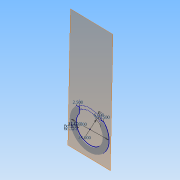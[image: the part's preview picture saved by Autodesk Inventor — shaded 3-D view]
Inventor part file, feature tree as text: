
AUTODESK INVENTOR PART (.ipt)
format: ipt  version: 2013 (Build 170138000, 138)  size: 106,496 bytes
history: native  units: in
note: dims shown in document units (in); Inventor stores cm internally (conversion verified against a paired STEP export)
features: extrude x2, plane x1, other x1, reference x1
ambient origin geometry x8: Origin, YZ Plane, XZ Plane, XY Plane, X Axis, Y Axis, Z Axis, Center Point
bodies: Solid1 (feature_tree)
feature tree (5):
  plane  "Work Plane1"
  other  "ThermoBulbBorder"
  extrude  "Sides"  Depth=24.0in
  extrude  "Extrusion2"  Depth=0.71in TaperAngle=0.0deg
  reference  "Reference2"
